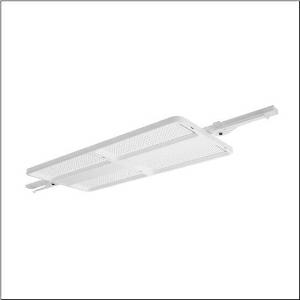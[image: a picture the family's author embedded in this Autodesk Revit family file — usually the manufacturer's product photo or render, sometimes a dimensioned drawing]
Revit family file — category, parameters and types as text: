
# Revit family: highbay_21_fur_modario_r__tragschiene_maxi_52hn12db5lma_777f
name_source: partatom
category: Lighting Fixtures
units: mm (PartAtom-declared; Revit-internal decimal feet)

## family parameters
Cut with Voids When Loaded = No
Host = Face
Light Source = No
Part Type = Normal
Room Calculation Point = No
Round Connector Dimension = Use Diameter
Shared = No

## types (1)
- --- (1 x LED, 4120 lm, 22.6 W, 5000K)
    Apparent Load = 23 VA
    CIE Flux Codes = 90 98 100 100 100
    Color Rendering = 80
    Color Temperature = 5000K
    Default Elevation = 1800 mm
    Description = high bay luminaire Highbay 21 for Modario® trunking rail maxi; direct symmetric wide distribution, light control with lens of PMMA; UGR ≤ 22 (X = 4H | Y = 8H | S = 0.25H | reflection values 70/50/20); luminous flux: 27.240lm; light colour: 850, colour temperature: 5000K, MacAdam ≤ 3 SDCM (initial), colour rendering: CRI > 80; luminous efficacy: 189,2lm/W; rated service life: 75.000h (L80/B50) at AT= ta max; control: DALI 2; luminaire connection: plug, 5-pole, with phase selectionmains connection: 230..240V, AC 50/60Hz; connected load: 144W; protection rating (complete): IP64; insulation class (complete): insulation class I (protective earthing); protection symbol: D; impact resistance: IK07; certification: CE, ENEC, VDE, UKCA; internal wiring halogen-free; luminaire corresponds to IFS (International Featured Standards) requirements for safety and quality in the food industry; LABS conformity tested according to VDMA 24364:2018-05; housing frame of high-performance plastic PA6, matt traffic white (RAL 9016); cover of PMMA; fixing on rail side of steel, galvanised, white; blank cover of PC, traffic white (RAL 9016); dimension (LxWxH): 1.496 x 442 x 72mm; permissible operating ambient temperature: -40..+55°C (reducing of maximum allowable ambient temperature of 5°C with ceiling mounting); packaging unit: 1 piece
    Height = 72 mm  [stored 0.23622 ft]
    Lamp = 1 x LED
    Lamp Light Flux = 4120 lm
    Lamp Power = 22.6 W
    Lamp count = 1
    Length = 946 mm
    Luminous efficacy = 182 lm/W
    Manufacturer = Siteco
    ModVariant = No
    Model = 52HN12DB5LMA
    Mounting Place = Ceiling
    Mounting Type = Pendant
    Number of Poles = 1
    OnlyDefault = Yes
    Power Factor = 1
    Product Name = Highbay 21 für Modario® Tragschiene maxi
    Product group = high bay luminaire
    ProductGroupID = 901
    Protection Class = Protection class I
    Protection Degree = IP 64
    RLX_Detail_Level = 1
    RLX_Emergency_Light_Flux = 0 lm
    RLX_Emergency_Type = 0
    RLX_Emergency_Type_DB = No
    RlxData = <blob elided: 127073 chars, md5=c03943fe>
    Socket = socket
    Standby Power = 0 W
    System Light Flux = 4120 lm
    System Power = 23 W
    Type Comments = : DC mode (central or group accumulator) initial emergency light level
    Type Image = l_1363248.jpg
    URL = http://relux.com
    VarID = @adj_002563
    Voltage = 0 V
    Weight = 0.00 kg
    Width = 442 mm

note: [stored X ft] marks values corroborated as IEEE doubles in the binary element streams (Revit-internal decimal feet)

## geometry (parser evidence)
native form markers: Blend x4, Sweep x10
no freeform markers — native parametric forms only
